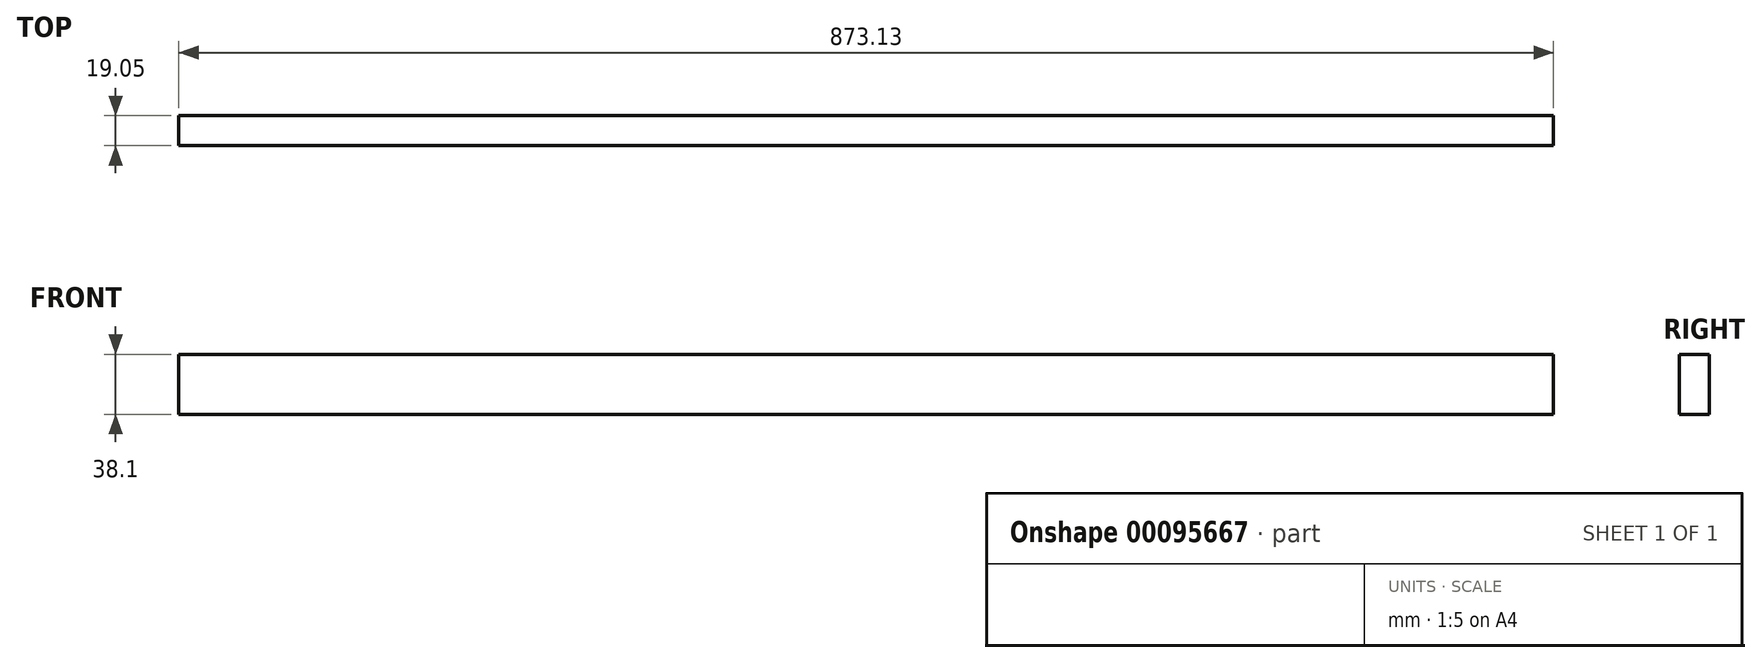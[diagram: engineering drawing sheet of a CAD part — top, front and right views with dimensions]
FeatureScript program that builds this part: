
annotation { "Feature Type Name" : "Feature", "Feature Type Description" : "" }
export const myFeature = defineFeature(function(context is Context, id is Id, definition is map)
    precondition{}
    {
        {
            var Q0;
            Q0=qCreatedBy(makeId("Front.planeOp"),FACE);
            var sketch = newSketch(context, id + "F0", { "sketchPlane" : qUnion([Q0])});
            skLineSegment(sketch, "E0.bottom", {"start": v(-468.5, -105.79) * mm, "end": v(404.63, -105.79) * mm});
            skLineSegment(sketch, "E0.top", {"start": v(-468.5, -143.89) * mm, "end": v(404.63, -143.89) * mm});
            skLineSegment(sketch, "E0.left", {"start": v(-468.5, -105.79) * mm, "end": v(-468.5, -143.89) * mm});
            skLineSegment(sketch, "E0.right", {"start": v(404.63, -105.79) * mm, "end": v(404.63, -143.89) * mm});
            skSolve(sketch);
        }
        {
            var Q0;
            Q0=makeQuery(id+"F0.imprint","IMPRINT",FACE,{"disambiguationData":[TD([[makeQuery(id+"F0.imprint","IMPRINT",EDGE,{"derivedFrom":sQuery(id+"F0.wireOp",EDGE,"E0.bottom")}),-1.0]])]});
            extrude(context, id + "F1", {"entities" : qUnion([Q0]), "depth" : 19.05 * mm});
        }
    });
